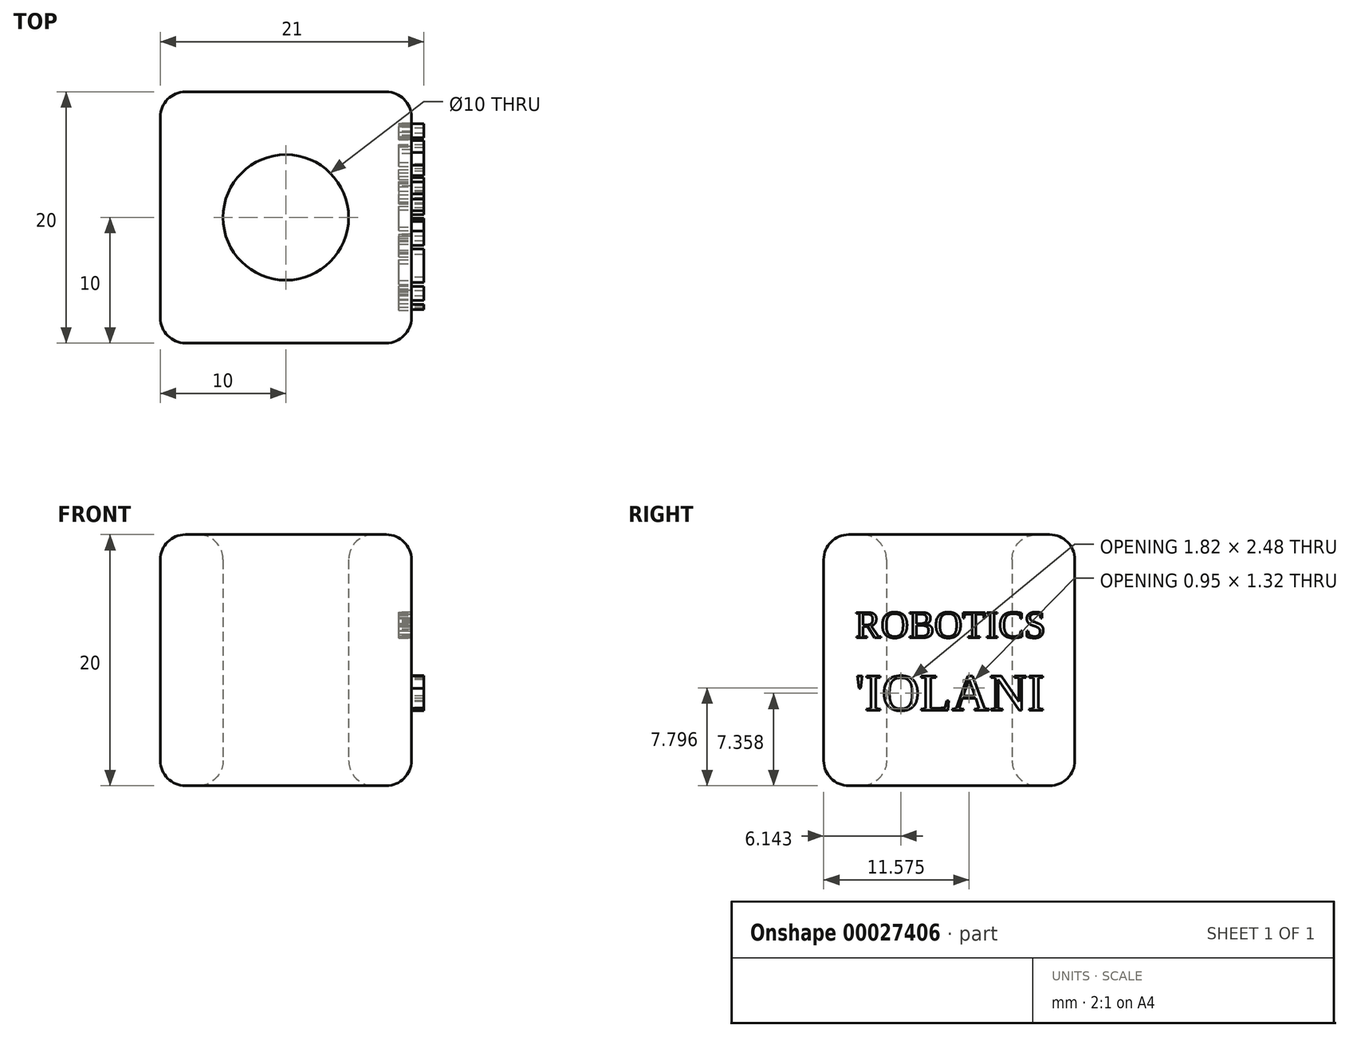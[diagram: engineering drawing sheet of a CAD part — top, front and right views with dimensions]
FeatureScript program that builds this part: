
annotation { "Feature Type Name" : "Feature", "Feature Type Description" : "" }
export const myFeature = defineFeature(function(context is Context, id is Id, definition is map)
    precondition{}
    {
        {
            var Q0;
            Q0=qCreatedBy(makeId("Top.planeOp"),FACE);
            var sketch = newSketch(context, id + "F0", { "sketchPlane" : qUnion([Q0])});
            skLineSegment(sketch, "E0.rect.bottom", {"start": v(10, 10) * mm, "end": v(-10, 10) * mm});
            skLineSegment(sketch, "E0.rect.top", {"start": v(10, -10) * mm, "end": v(-10, -10) * mm});
            skLineSegment(sketch, "E0.rect.left", {"start": v(10, 10) * mm, "end": v(10, -10) * mm});
            skLineSegment(sketch, "E0.rect.right", {"start": v(-10, 10) * mm, "end": v(-10, -10) * mm});
            skPoint(sketch, "E0.rect.middle", {"position": v(0, 0) * mm});
            skCircle(sketch, "E1", {"center": v(0, 0) * mm, "radius": 5 * mm});
            skSolve(sketch);
        }
        {
            var Q0;
            Q0=makeQuery(id+"F0.imprint","IMPRINT",FACE,{"disambiguationData":[TD([[makeQuery(id+"F0.imprint","IMPRINT",EDGE,{"derivedFrom":sQuery(id+"F0.wireOp",EDGE,"E0.rect.bottom")}),1.0]])]});
            extrude(context, id + "F1", {"entities" : qUnion([Q0]), "depth" : 20 * mm});
        }
        {
            var Q0;
            Q0=makeQuery(id+"F1.opExtrude","CAP_FACE",FACE,{"disambiguationData":[OSD([sQuery(id+"F0.wireOp",EDGE,"E0.rect.bottom"),sQuery(id+"F0.wireOp",EDGE,"E0.rect.top"),sQuery(id+"F0.wireOp",EDGE,"E0.rect.left"),sQuery(id+"F0.wireOp",EDGE,"E0.rect.right"),sQuery(id+"F0.wireOp",EDGE,"E1")])],"isStart":false});
            var Q1;
            Q1=makeQuery(id+"F1.opExtrude","SWEPT_FACE",FACE,{"disambiguationData":[OSD([sQuery(id+"F0.wireOp",EDGE,"E0.rect.right")])]});
            var Q2;
            Q2=makeQuery(id+"F1.opExtrude","SWEPT_FACE",FACE,{"disambiguationData":[OSD([sQuery(id+"F0.wireOp",EDGE,"E0.rect.left")])]});
            var Q3;
            Q3=makeQuery(id+"F1.opExtrude","SWEPT_FACE",FACE,{"disambiguationData":[OSD([sQuery(id+"F0.wireOp",EDGE,"E0.rect.top")])]});
            var Q4;
            Q4=makeQuery(id+"F1.opExtrude","CAP_FACE",FACE,{"disambiguationData":[OSD([sQuery(id+"F0.wireOp",EDGE,"E0.rect.bottom"),sQuery(id+"F0.wireOp",EDGE,"E0.rect.top"),sQuery(id+"F0.wireOp",EDGE,"E0.rect.left"),sQuery(id+"F0.wireOp",EDGE,"E0.rect.right"),sQuery(id+"F0.wireOp",EDGE,"E1")])],"isStart":true});
            fillet(context, id + "F2", {"entities" : qUnion([Q0, Q1, Q2, Q3, Q4]), "radius" : 2 * mm, "tangentPropagation" : true, "allowEdgeOverflow" : false});
        }
        {
            var Q0;
            Q0=makeQuery(id+"F1.opExtrude","SWEPT_FACE",FACE,{"disambiguationData":[OSD([sQuery(id+"F0.wireOp",EDGE,"E0.rect.left")])]});
            var sketch = newSketch(context, id + "F3", { "sketchPlane" : qUnion([Q0])});
            skText(sketch, "E2", { "text": "ROBOTICS", "fontName": "Tinos-Regular.ttf"});
            const initialGuessF3  = {"E2": [-0.0075, 0.01179, 1, 0, 0.00221]};
            skSetInitialGuess(sketch, initialGuessF3);
            skSolve(sketch);
        }
        {
            var Q0;
            Q0 = qSketchRegion(id + "F3", true);
            extrude(context, id + "F4", {"entities" : qUnion([Q0]), "operationType" : NewBodyOperationType.REMOVE, "oppositeDirection" : true, "depth" : 1 * mm});
        }
        {
            var Q0;
            {var subQ0=sQuery(id+"F0.wireOp",EDGE,"E0.rect.left");Q0=makeQuery(id+"F4.boolean.opBoolean","SPLIT",FACE,{"disambiguationData":[TD([makeQuery(id+"F4.opExtrude","SWEPT_FACE",FACE,{"disambiguationData":[OSD([sQuery(id+"F3.wireOp",EDGE,"E2.sketch_text.stroke-0")])]})])],"derivedFrom":makeQuery(id+"F1.opExtrude","SWEPT_FACE",FACE,{"disambiguationData":[OSD([subQ0])]})});}
            var sketch = newSketch(context, id + "F5", { "sketchPlane" : qUnion([Q0])});
            skText(sketch, "E3", { "text": "\'IOLANI", "fontName": "Tinos-Regular.ttf"});
            skPoint(sketch, "E4", {"position": v(0, 2) * mm});
            const initialGuessF5  = {"E3": [-0.0075, 0.006, 1, 0, 0.003]};
            skSetInitialGuess(sketch, initialGuessF5);
            skSolve(sketch);
        }
        {
            var Q0;
            Q0 = qSketchRegion(id + "F5", true);
            extrude(context, id + "F6", {"entities" : qUnion([Q0]), "depth" : 1 * mm});
        }
    });
